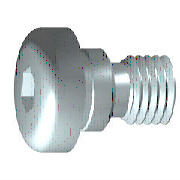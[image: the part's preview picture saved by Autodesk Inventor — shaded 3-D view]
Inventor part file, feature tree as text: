
AUTODESK INVENTOR PART (.ipt)
format: ipt  version: 2020 (Build 240168000, 168)  size: 226,816 bytes
history: native  units: mm (DEFAULTED — no unit token found)
features: sketch x2, other x2, extrude x1
ambient origin geometry x7: Origin, YZ Plane, XZ Plane, X Axis, Y Axis, Z Axis, Center Point
bodies: Solid1 (feature_tree), Body (feature_tree)
feature tree (5):
  sketch  "Sketch1"  dims[d0=4.826mm d1=6.2992mm]
  extrude  "Slot"  Depth=6.2992mm
  other  "Groove1"
  other  "Groove2"
  sketch  "Sketch2"  dims[d2=9.525mm d3=3.666174mm d5=9.525mm d6=4.7752mm d7=2.3876mm d8=60.0deg d9=17.4625mm d10=90.0deg d11=10.0mm d12=0.0mm d13=2.3622mm d14=0.62992mm d15=0.62992mm d16=0.127mm d17=45.0deg d19=45.0deg d20=5.7658mm d21=3.56616mm d22=45.0deg d23=2.1082mm d25=9.525mm d26=0.0mm d27=90.0deg d29=0.0mm d30=90.0deg d31=45.0deg d32=0.7366mm d33=0.0mm d34=2.3622mm d35=0.0mm]
